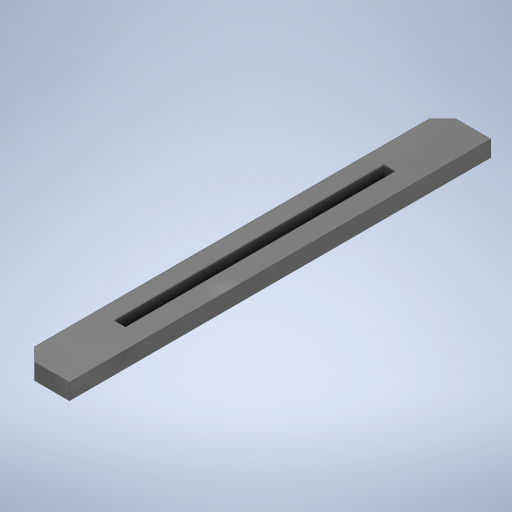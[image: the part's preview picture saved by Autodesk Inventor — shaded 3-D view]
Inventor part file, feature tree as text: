
AUTODESK INVENTOR PART (.ipt)
format: ipt  version: 2024 (Build 280153000, 153)  size: 267,264 bytes
history: native  units: in
note: dims shown in document units (in); Inventor stores cm internally (conversion verified against a paired STEP export)
features: extrude x3, sketch x3
ambient origin geometry x8: Origin, YZ Plane, XZ Plane, XY Plane, X Axis, Y Axis, Z Axis, Center Point
bodies: Solid1 (feature_tree)
feature tree (6):
  extrude  "Extrusion1"  Depth=0.0236in TaperAngle=0.0deg
  extrude  "Extrusion2"  Depth=0.3976in
  extrude  "Extrusion3"  Depth=0.0337in
  sketch  "Sketch1"  dims[d0=0.622in d1=0.0236in d2=0.0in]
  sketch  "Sketch2"  dims[d3=0.0161in d4=0.3976in]
  sketch  "Sketch3"  dims[d5=0.0in d6=0.0in d7=0.0337in d8=0.0376in d9=0.0197in d10=0.0197in d11=0.0197in d12=0.0197in d13=0.0in d14=0.0in]
